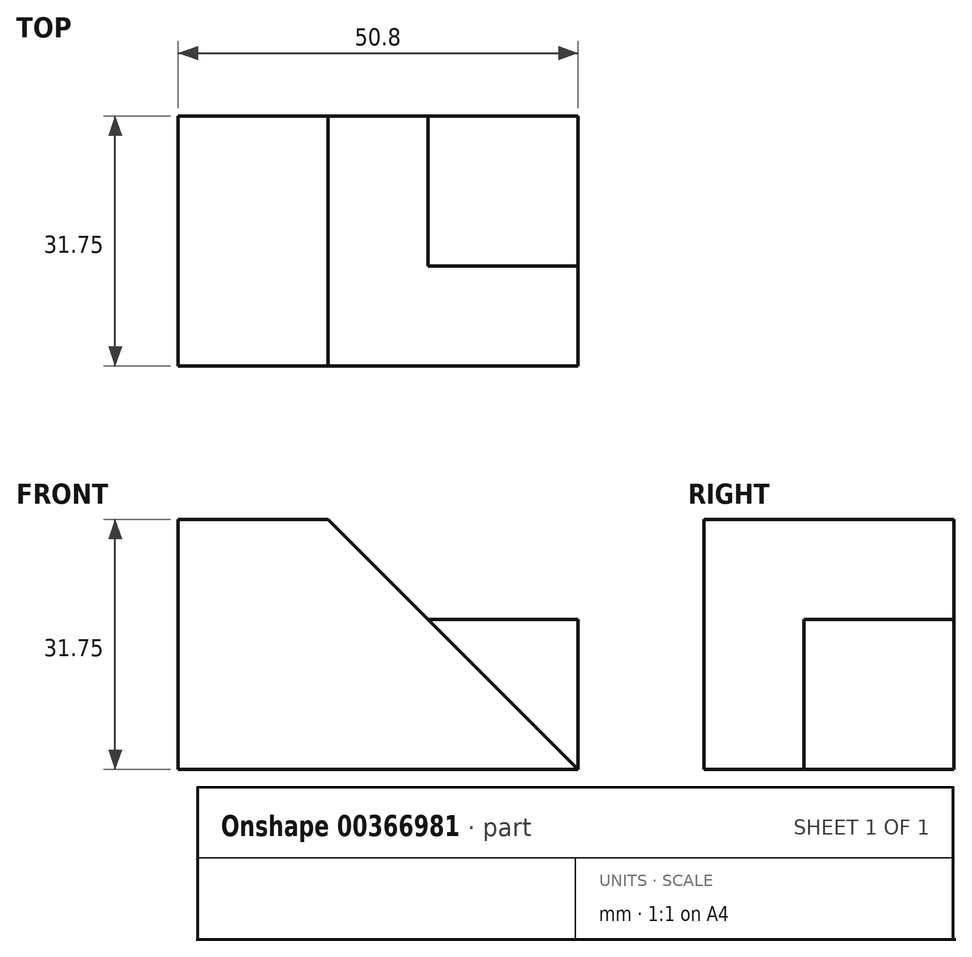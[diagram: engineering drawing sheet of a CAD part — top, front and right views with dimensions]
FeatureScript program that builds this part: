
annotation { "Feature Type Name" : "Feature", "Feature Type Description" : "" }
export const myFeature = defineFeature(function(context is Context, id is Id, definition is map)
    precondition{}
    {
        {
            var Q0;
            Q0=qCreatedBy(makeId("Front.planeOp"),FACE);
            var sketch = newSketch(context, id + "F0", { "sketchPlane" : qUnion([Q0])});
            skLineSegment(sketch, "E0", {"start": v(0, 0) * mm, "end": v(50.8, 0) * mm});
            skLineSegment(sketch, "E1", {"start": v(50.8, 0) * mm, "end": v(50.8, 19.05) * mm});
            skLineSegment(sketch, "E2", {"start": v(50.8, 19.05) * mm, "end": v(31.75, 19.05) * mm});
            skLineSegment(sketch, "E3", {"start": v(31.75, 19.05) * mm, "end": v(31.75, 31.75) * mm});
            skLineSegment(sketch, "E4", {"start": v(31.75, 31.75) * mm, "end": v(0, 31.75) * mm});
            skLineSegment(sketch, "E5", {"start": v(0, 31.75) * mm, "end": v(0, 0) * mm});
            skSolve(sketch);
        }
        {
            var Q0;
            Q0=makeQuery(id+"F0.imprint","IMPRINT",FACE,{"disambiguationData":[TD([[makeQuery(id+"F0.imprint","IMPRINT",EDGE,{"derivedFrom":sQuery(id+"F0.wireOp",EDGE,"E0")}),1.0]])]});
            extrude(context, id + "F1", {"entities" : qUnion([Q0]), "depth" : 31.75 * mm});
        }
        {
            var Q0;
            Q0=makeQuery(id+"F1.opExtrude","CAP_FACE",FACE,{"disambiguationData":[OSD([sQuery(id+"F0.wireOp",EDGE,"E0"),sQuery(id+"F0.wireOp",EDGE,"E1"),sQuery(id+"F0.wireOp",EDGE,"E2"),sQuery(id+"F0.wireOp",EDGE,"E3"),sQuery(id+"F0.wireOp",EDGE,"E4"),sQuery(id+"F0.wireOp",EDGE,"E5")])],"isStart":false});
            var sketch = newSketch(context, id + "F2", { "sketchPlane" : qUnion([Q0])});
            skLineSegment(sketch, "E6", {"start": v(31.75, 19.05) * mm, "end": v(19.05, 31.75) * mm});
            skSolve(sketch);
        }
        {
            var Q0;
            {var subQ0=sQuery(id+"F2.wireOp",EDGE,"E6");Q0=makeQuery(id+"F2.imprint","IMPRINT",FACE,{"disambiguationData":[TD([[makeQuery(id+"F2.imprint","IMPRINT",EDGE,{"derivedFrom":subQ0}),-1.0]])]});}
            extrude(context, id + "F3", {"entities" : qUnion([Q0]), "operationType" : NewBodyOperationType.REMOVE, "oppositeDirection" : true, "depth" : 31.75 * mm});
        }
        {
            var Q0;
            Q0=makeQuery(id+"F1.opExtrude","CAP_FACE",FACE,{"disambiguationData":[OSD([sQuery(id+"F0.wireOp",EDGE,"E0"),sQuery(id+"F0.wireOp",EDGE,"E1"),sQuery(id+"F0.wireOp",EDGE,"E2"),sQuery(id+"F0.wireOp",EDGE,"E3"),sQuery(id+"F0.wireOp",EDGE,"E4"),sQuery(id+"F0.wireOp",EDGE,"E5")])],"isStart":false});
            var sketch = newSketch(context, id + "F4", { "sketchPlane" : qUnion([Q0])});
            skLineSegment(sketch, "E7", {"start": v(31.75, 19.05) * mm, "end": v(50.8, 0) * mm});
            skSolve(sketch);
        }
        {
            var Q0;
            Q0=makeQuery(id+"F4.imprint","IMPRINT",FACE,{"disambiguationData":[TD([[makeQuery(id+"F4.imprint","IMPRINT",EDGE,{"derivedFrom":sQuery(id+"F4.wireOp",EDGE,"E7")}),1.0]])]});
            extrude(context, id + "F5", {"entities" : qUnion([Q0]), "operationType" : NewBodyOperationType.REMOVE, "oppositeDirection" : true, "depth" : 12.7 * mm});
        }
    });
